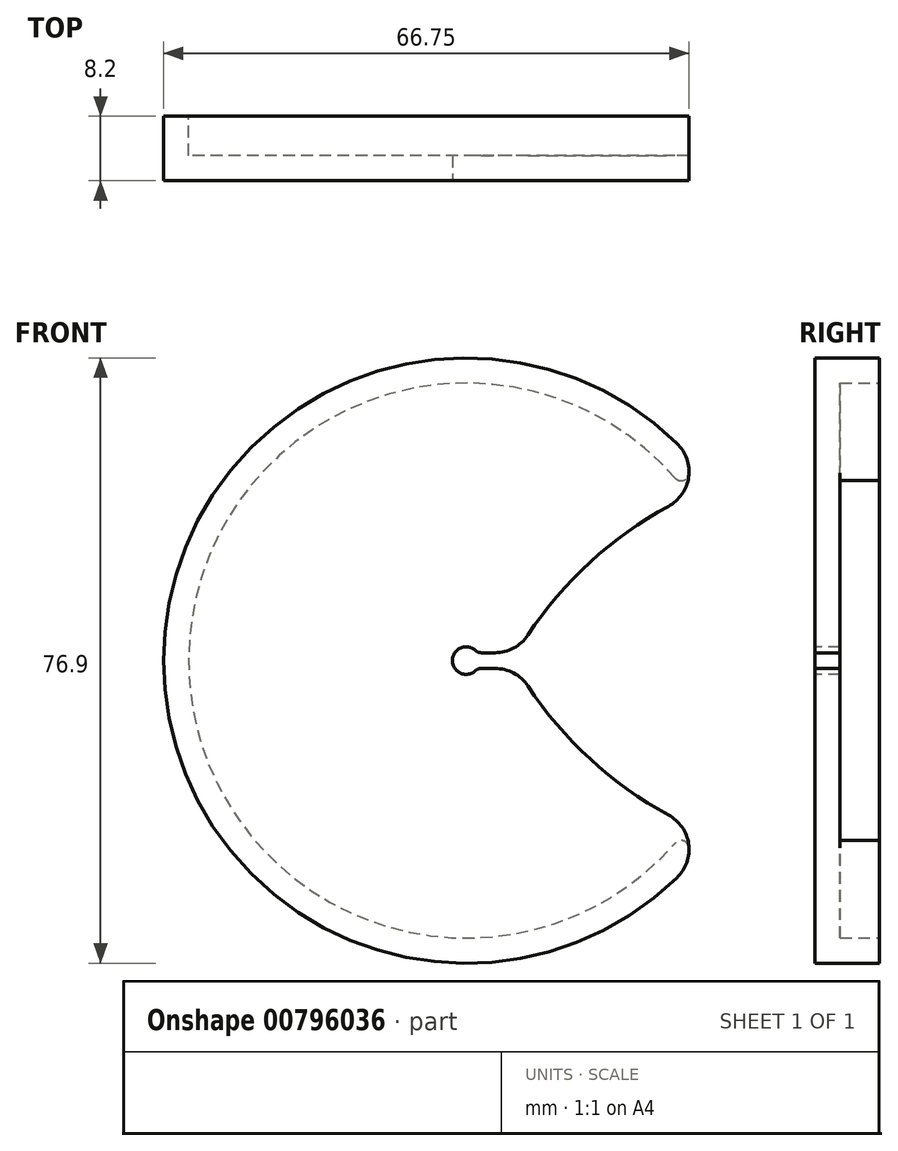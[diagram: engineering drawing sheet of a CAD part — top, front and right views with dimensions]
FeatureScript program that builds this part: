
annotation { "Feature Type Name" : "Feature", "Feature Type Description" : "" }
export const myFeature = defineFeature(function(context is Context, id is Id, definition is map)
    precondition{}
    {
        {
            var Q0;
            Q0=qCreatedBy(makeId("Front.planeOp"),FACE);
            var sketch = newSketch(context, id + "F0", { "sketchPlane" : qUnion([Q0])});
            skCircle(sketch, "E0", {"center": v(0, 0) * mm, "radius": 38.45 * mm});
            skCircle(sketch, "E1", {"center": v(0, 0) * mm, "radius": 35.25 * mm});
            skSolve(sketch);
        }
        {
            var Q0;
            Q0 = qSketchRegion(id + "F0", true);
            extrude(context, id + "F1", {"entities" : qUnion([Q0]), "depth" : 5 * mm, "offsetDistance" : 25 * mm});
        }
        {
            var Q0;
            Q0=makeQuery(id+"F1.opExtrude","CAP_FACE",FACE,{"disambiguationData":[OSD([sQuery(id+"F0.wireOp",EDGE,"E0"),sQuery(id+"F0.wireOp",EDGE,"E1")])],"isStart":false});
            var sketch = newSketch(context, id + "F2", { "sketchPlane" : qUnion([Q0])});
            skCircle(sketch, "E2", {"center": v(0, 0) * mm, "radius": 38.45 * mm});
            skSolve(sketch);
        }
        {
            var Q0;
            Q0 = qSketchRegion(id + "F2", true);
            extrude(context, id + "F3", {"entities" : qUnion([Q0]), "operationType" : NewBodyOperationType.ADD, "depth" : 3.2 * mm, "offsetDistance" : 25 * mm});
        }
        {
            var Q0;
            Q0=makeQuery(id+"F3.opExtrude","CAP_FACE",FACE,{"disambiguationData":[OSD([sQuery(id+"F2.wireOp",EDGE,"E2")])],"isStart":false});
            var sketch = newSketch(context, id + "F4", { "sketchPlane" : qUnion([Q0])});
            skArc(sketch, "E3", {"start": v(1.44, 1) * mm, "mid": v(-1.75, 0) * mm, "end": v(1.44, -1) * mm});
            skLineSegment(sketch, "E4", {"start": v(1.44, 1) * mm, "end": v(6.44, 1) * mm});
            skLineSegment(sketch, "E5", {"start": v(1.44, -1) * mm, "end": v(6.44, -1) * mm});
            skArc(sketch, "E6", {"start": v(41.44, 25) * mm, "mid": v(21.26, 16.9) * mm, "end": v(6.44, 1) * mm});
            skLineSegment(sketch, "E7", {"start": v(0, 0) * mm, "end": v(43.5, 0) * mm, "construction": true});
            skArc(sketch, "E8.MirrorCS", {"start": v(41.44, -25) * mm, "mid": v(21.26, -16.9) * mm, "end": v(6.44, -1) * mm});
            skLineSegment(sketch, "E9", {"start": v(41.44, 25) * mm, "end": v(41.44, -25) * mm});
            skSolve(sketch);
        }
        {
            var Q0;
            Q0 = qSketchRegion(id + "F4", true);
            extrude(context, id + "F5", {"entities" : qUnion([Q0]), "operationType" : NewBodyOperationType.REMOVE, "oppositeDirection" : true, "depth" : 25 * mm, "offsetDistance" : 25 * mm});
        }
        {
            var Q0;
            Q0=makeQuery(id+"F5.boolean.opBoolean","INTERSECT",EDGE,{"derivedFrom":[makeQuery(id+"F3.boolean.opBoolean","MERGE",FACE,{"derivedFrom":[makeQuery(id+"F1.opExtrude","SWEPT_FACE",FACE,{"disambiguationData":[OSD([sQuery(id+"F0.wireOp",EDGE,"E0")])]}),makeQuery(id+"F3.opExtrude","SWEPT_FACE",FACE,{"disambiguationData":[OSD([sQuery(id+"F2.wireOp",EDGE,"E2")])]})]}),makeQuery(id+"F5.opExtrude","SWEPT_FACE",FACE,{"disambiguationData":[OSD([sQuery(id+"F4.wireOp",EDGE,"E6")])]})]});
            var Q1;
            Q1=makeQuery(id+"F5.boolean.opBoolean","INTERSECT",EDGE,{"derivedFrom":[makeQuery(id+"F3.boolean.opBoolean","MERGE",FACE,{"derivedFrom":[makeQuery(id+"F1.opExtrude","SWEPT_FACE",FACE,{"disambiguationData":[OSD([sQuery(id+"F0.wireOp",EDGE,"E0")])]}),makeQuery(id+"F3.opExtrude","SWEPT_FACE",FACE,{"disambiguationData":[OSD([sQuery(id+"F2.wireOp",EDGE,"E2")])]})]}),makeQuery(id+"F5.opExtrude","SWEPT_FACE",FACE,{"disambiguationData":[OSD([sQuery(id+"F4.wireOp",EDGE,"E8.MirrorCS")])]})]});
            var Q2;
            Q2=makeQuery(id+"F5.boolean.opBoolean","COPY",EDGE,{"derivedFrom":makeQuery(id+"F5.opExtrude","SWEPT_EDGE",EDGE,{"disambiguationData":[OSD([sQuery(id+"F4.wireOp",EDGE,"E5"),sQuery(id+"F4.wireOp",EDGE,"E8.MirrorCS")])]})});
            var Q3;
            Q3=makeQuery(id+"F5.boolean.opBoolean","COPY",EDGE,{"derivedFrom":makeQuery(id+"F5.opExtrude","SWEPT_EDGE",EDGE,{"disambiguationData":[OSD([sQuery(id+"F4.wireOp",EDGE,"E4"),sQuery(id+"F4.wireOp",EDGE,"E6")])]})});
            fillet(context, id + "F6", {"entities" : qUnion([Q0, Q1, Q2, Q3]), "radius" : 5 * mm, "tangentPropagation" : true, "allowEdgeOverflow" : false});
        }
        {
            var Q0;
            Q0=makeQuery(id+"F5.boolean.opBoolean","COPY",EDGE,{"derivedFrom":makeQuery(id+"F5.opExtrude","SWEPT_EDGE",EDGE,{"disambiguationData":[OSD([sQuery(id+"F4.wireOp",EDGE,"E3"),sQuery(id+"F4.wireOp",EDGE,"E4")])]})});
            var Q1;
            Q1=makeQuery(id+"F5.boolean.opBoolean","COPY",EDGE,{"derivedFrom":makeQuery(id+"F5.opExtrude","SWEPT_EDGE",EDGE,{"disambiguationData":[OSD([sQuery(id+"F4.wireOp",EDGE,"E3"),sQuery(id+"F4.wireOp",EDGE,"E5")])]})});
            var Q2;
            Q2=makeQuery(id+"F6.opFillet","BLEND_EDGE",EDGE,{"blendedFrom":[makeQuery(id+"F5.boolean.opBoolean","INTERSECT",EDGE,{"derivedFrom":[makeQuery(id+"F3.boolean.opBoolean","MERGE",FACE,{"derivedFrom":[makeQuery(id+"F1.opExtrude","SWEPT_FACE",FACE,{"disambiguationData":[OSD([sQuery(id+"F0.wireOp",EDGE,"E0")])]}),makeQuery(id+"F3.opExtrude","SWEPT_FACE",FACE,{"disambiguationData":[OSD([sQuery(id+"F2.wireOp",EDGE,"E2")])]})]}),makeQuery(id+"F5.opExtrude","SWEPT_FACE",FACE,{"disambiguationData":[OSD([sQuery(id+"F4.wireOp",EDGE,"E6")])]})]}),makeQuery(id+"F1.opExtrude","SWEPT_FACE",FACE,{"disambiguationData":[OSD([sQuery(id+"F0.wireOp",EDGE,"E1")])]})],"blendedInto":[makeQuery(id+"F1.opExtrude","SWEPT_FACE",FACE,{"disambiguationData":[OSD([sQuery(id+"F0.wireOp",EDGE,"E1")])]})]});
            var Q3;
            Q3=makeQuery(id+"F6.opFillet","BLEND_EDGE",EDGE,{"blendedFrom":[makeQuery(id+"F5.boolean.opBoolean","INTERSECT",EDGE,{"derivedFrom":[makeQuery(id+"F3.boolean.opBoolean","MERGE",FACE,{"derivedFrom":[makeQuery(id+"F1.opExtrude","SWEPT_FACE",FACE,{"disambiguationData":[OSD([sQuery(id+"F0.wireOp",EDGE,"E0")])]}),makeQuery(id+"F3.opExtrude","SWEPT_FACE",FACE,{"disambiguationData":[OSD([sQuery(id+"F2.wireOp",EDGE,"E2")])]})]}),makeQuery(id+"F5.opExtrude","SWEPT_FACE",FACE,{"disambiguationData":[OSD([sQuery(id+"F4.wireOp",EDGE,"E8.MirrorCS")])]})]}),makeQuery(id+"F1.opExtrude","SWEPT_FACE",FACE,{"disambiguationData":[OSD([sQuery(id+"F0.wireOp",EDGE,"E1")])]})],"blendedInto":[makeQuery(id+"F1.opExtrude","SWEPT_FACE",FACE,{"disambiguationData":[OSD([sQuery(id+"F0.wireOp",EDGE,"E1")])]})]});
            fillet(context, id + "F7", {"entities" : qUnion([Q0, Q1, Q2, Q3]), "radius" : 1 * mm, "tangentPropagation" : true, "allowEdgeOverflow" : false});
        }
    });
